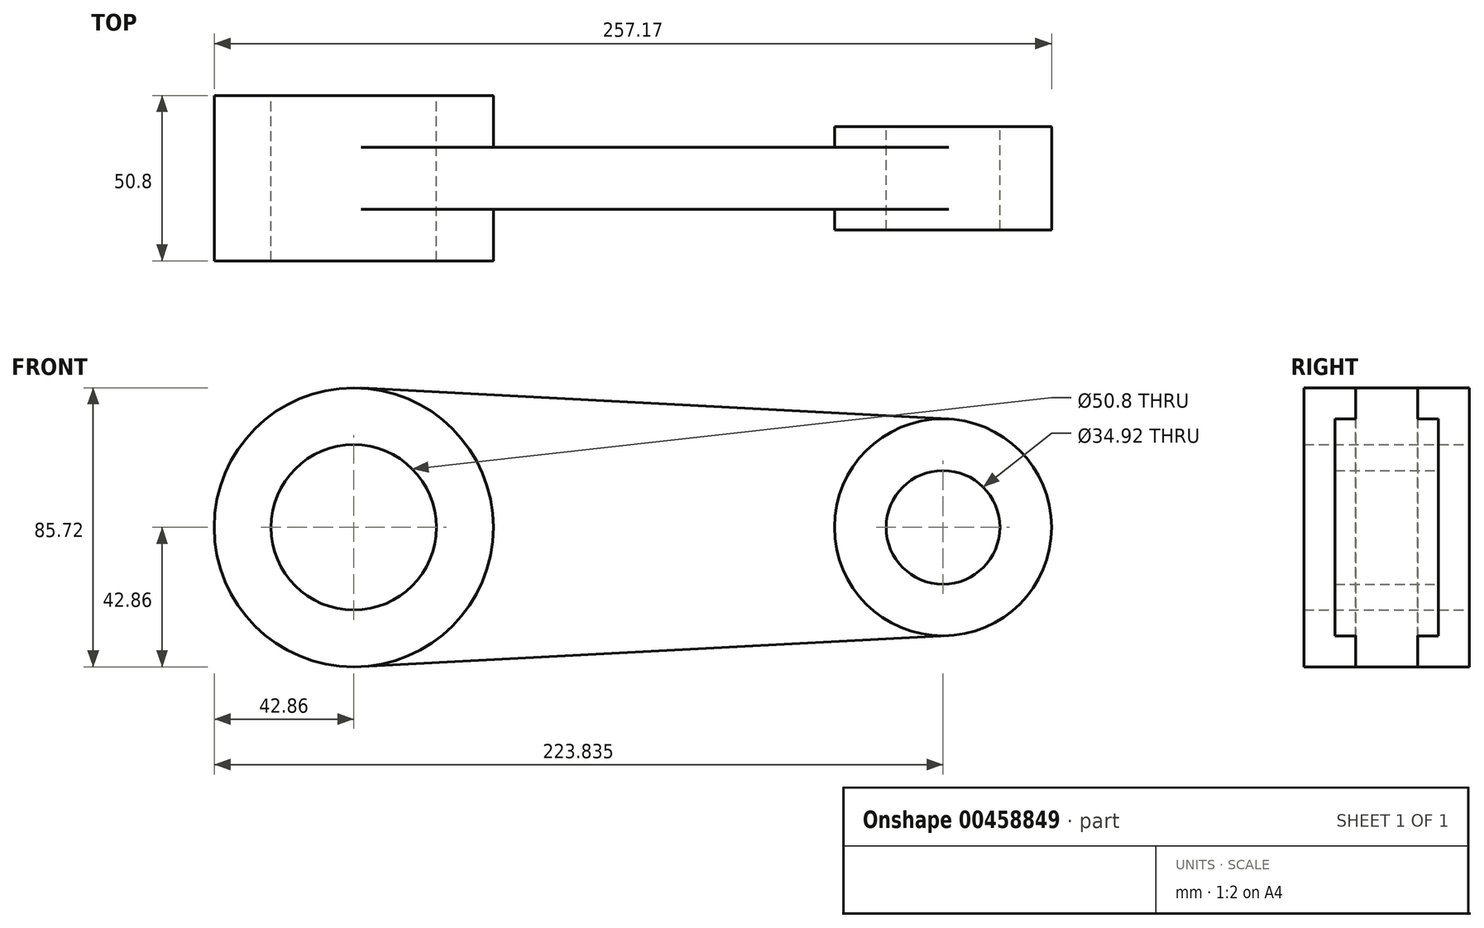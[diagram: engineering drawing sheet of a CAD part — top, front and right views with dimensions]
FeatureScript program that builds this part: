
annotation { "Feature Type Name" : "Feature", "Feature Type Description" : "" }
export const myFeature = defineFeature(function(context is Context, id is Id, definition is map)
    precondition{}
    {
        {
            var Q0;
            Q0=qCreatedBy(makeId("Front.planeOp"),FACE);
            var sketch = newSketch(context, id + "F0", { "sketchPlane" : qUnion([Q0])});
            skCircle(sketch, "E0", {"center": v(0, 0) * mm, "radius": 25.4 * mm});
            skCircle(sketch, "E1", {"center": v(0, 0) * mm, "radius": 42.86 * mm});
            skCircle(sketch, "E2", {"center": v(180.98, 0) * mm, "radius": 17.46 * mm});
            skCircle(sketch, "E3", {"center": v(180.98, 0) * mm, "radius": 33.34 * mm});
            skLineSegment(sketch, "E4", {"start": v(2.26, -42.8) * mm, "end": v(182.73, -33.3) * mm});
            skLineSegment(sketch, "E5", {"start": v(2.26, 42.8) * mm, "end": v(182.73, 33.3) * mm});
            skSolve(sketch);
        }
        {
            var Q0;
            Q0=makeQuery(id+"F0.imprint","IMPRINT",FACE,{"disambiguationData":[TD([[makeQuery(id+"F0.imprint","IMPRINT",EDGE,{"derivedFrom":sQuery(id+"F0.wireOp",EDGE,"E0")}),-1.0]])]});
            extrude(context, id + "F1", {"entities" : qUnion([Q0]), "depth" : 50.8 * mm, "symmetric" : true});
        }
        {
            var Q0;
            {var subQ0=sQuery(id+"F0.wireOp",EDGE,"eR6GLvmT-agu1-3Djh-gmzt-1HRNs2KsTib9");var subQ1=sQuery(id+"F0.wireOp",EDGE,"E1");var subQ2=makeQuery(id+"F0.imprint","INTERSECT",VERTEX,{"disambiguationData":[OD(1.0)],"derivedFrom":[subQ1,subQ0]});Q0=makeQuery(id+"F0.imprint","IMPRINT",FACE,{"disambiguationData":[TD([[makeQuery(id+"F0.imprint","IMPRINT",EDGE,{"disambiguationData":[TD([[subQ2,1.0]])],"derivedFrom":subQ1}),-1.0]])]});}
            extrude(context, id + "F2", {"entities" : qUnion([Q0]), "operationType" : NewBodyOperationType.ADD, "depth" : 19.05 * mm, "symmetric" : true});
        }
        {
            var Q0;
            Q0=makeQuery(id+"F0.imprint","IMPRINT",FACE,{"disambiguationData":[TD([[makeQuery(id+"F0.imprint","IMPRINT",EDGE,{"derivedFrom":sQuery(id+"F0.wireOp",EDGE,"E2")}),-1.0]])]});
            extrude(context, id + "F3", {"entities" : qUnion([Q0]), "operationType" : NewBodyOperationType.ADD, "depth" : 31.75 * mm, "symmetric" : true});
        }
    });
